# Revit family: Faucet-Tub_and_Whirlpool-Delta-Tesla-Floor_Mounted-4752
name_source: partatom
category: Plumbing Fixtures
revit_build: Autodesk Revit MEP 2012 (Build: 20110916_2132(x64)
units: mm (PartAtom-declared; Revit-internal decimal feet)

## types (1)
- Standard
    Cold Water Radius = 0.188 "
    Cold Water Supply Flow = 0 GPM
    Date Modified = January 5, 2015
    Depth = 12.5 "
    Description = Tesla Roman Tub/Whirlpool Floor Mounted Faucet Trim With Hand Shower
    Equipment Abbreviation = FT
    Family Version = 1.0
    Height = 41.86 "
    Hot Water Radius = 0.188 "
    Hot Water Supply Flow = 0 GPM
    Manufacturer = Delta Faucet Company
    Model = T4752-fl
    Model Disclaimer = Contact Delta Faucet Company for More Information
    Product Material = Steel - Delta Faucet Company - Stainless
    URL = http://www.deltafaucet.com
    Width = 11.125 "
    zz Integer 1 = 4752

## geometry (parser evidence)
native form markers: Blend x4, Sweep x2
no freeform markers — native parametric forms only
